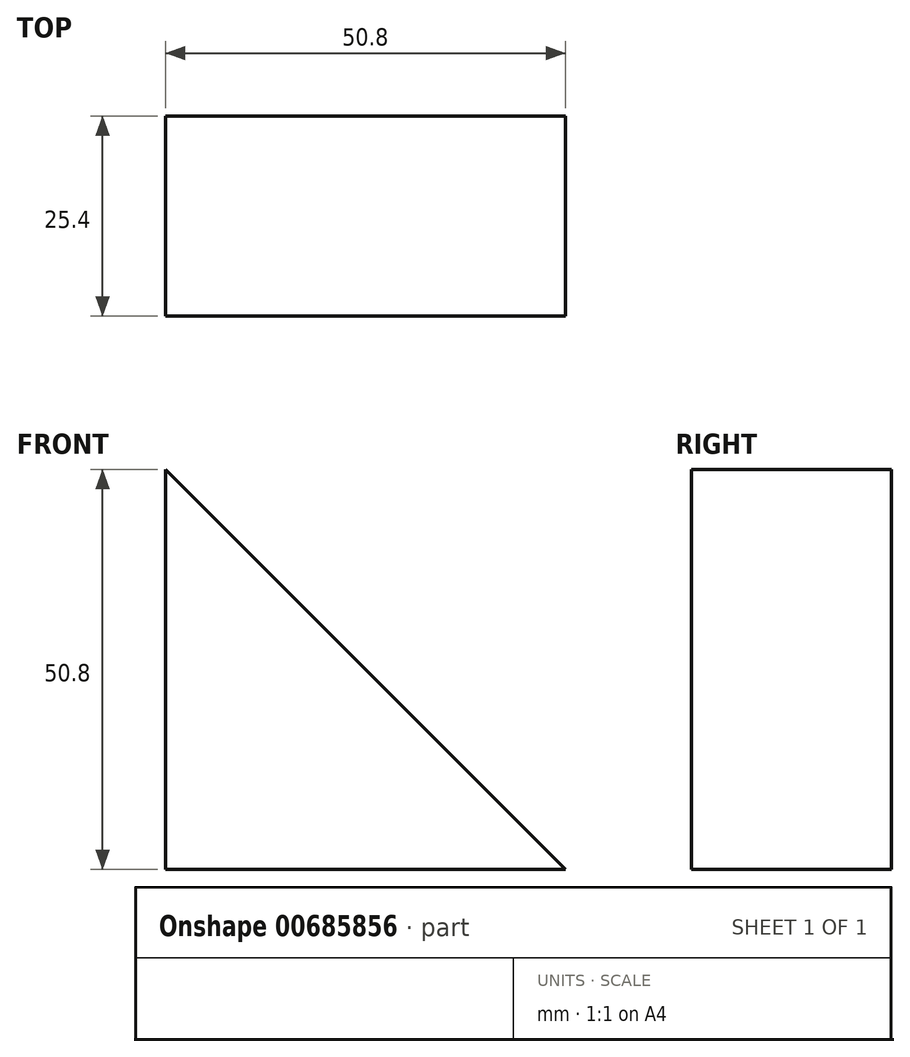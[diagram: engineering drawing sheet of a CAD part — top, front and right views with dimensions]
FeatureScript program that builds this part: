
annotation { "Feature Type Name" : "Feature", "Feature Type Description" : "" }
export const myFeature = defineFeature(function(context is Context, id is Id, definition is map)
    precondition{}
    {
        {
            var Q0;
            Q0=qCreatedBy(makeId("Front.planeOp"),FACE);
            var sketch = newSketch(context, id + "F0", { "sketchPlane" : qUnion([Q0])});
            skLineSegment(sketch, "E0.top", {"start": v(1.24, -35.8) * mm, "end": v(52.04, -35.8) * mm});
            skLineSegment(sketch, "E0.left", {"start": v(1.24, 15) * mm, "end": v(1.24, -35.8) * mm});
            skLineSegment(sketch, "E1", {"start": v(1.24, 15) * mm, "end": v(52.04, -35.8) * mm});
            skSolve(sketch);
        }
        {
            var Q0;
            Q0=makeQuery(id+"F0.imprint","IMPRINT",FACE,{"disambiguationData":[TD([[makeQuery(id+"F0.imprint","IMPRINT",EDGE,{"derivedFrom":sQuery(id+"F0.wireOp",EDGE,"E0.top")}),1.0]])]});
            extrude(context, id + "F1", {"entities" : qUnion([Q0]), "depth" : 25.4 * mm, "offsetDistance" : 25.4 * mm});
        }
    });
